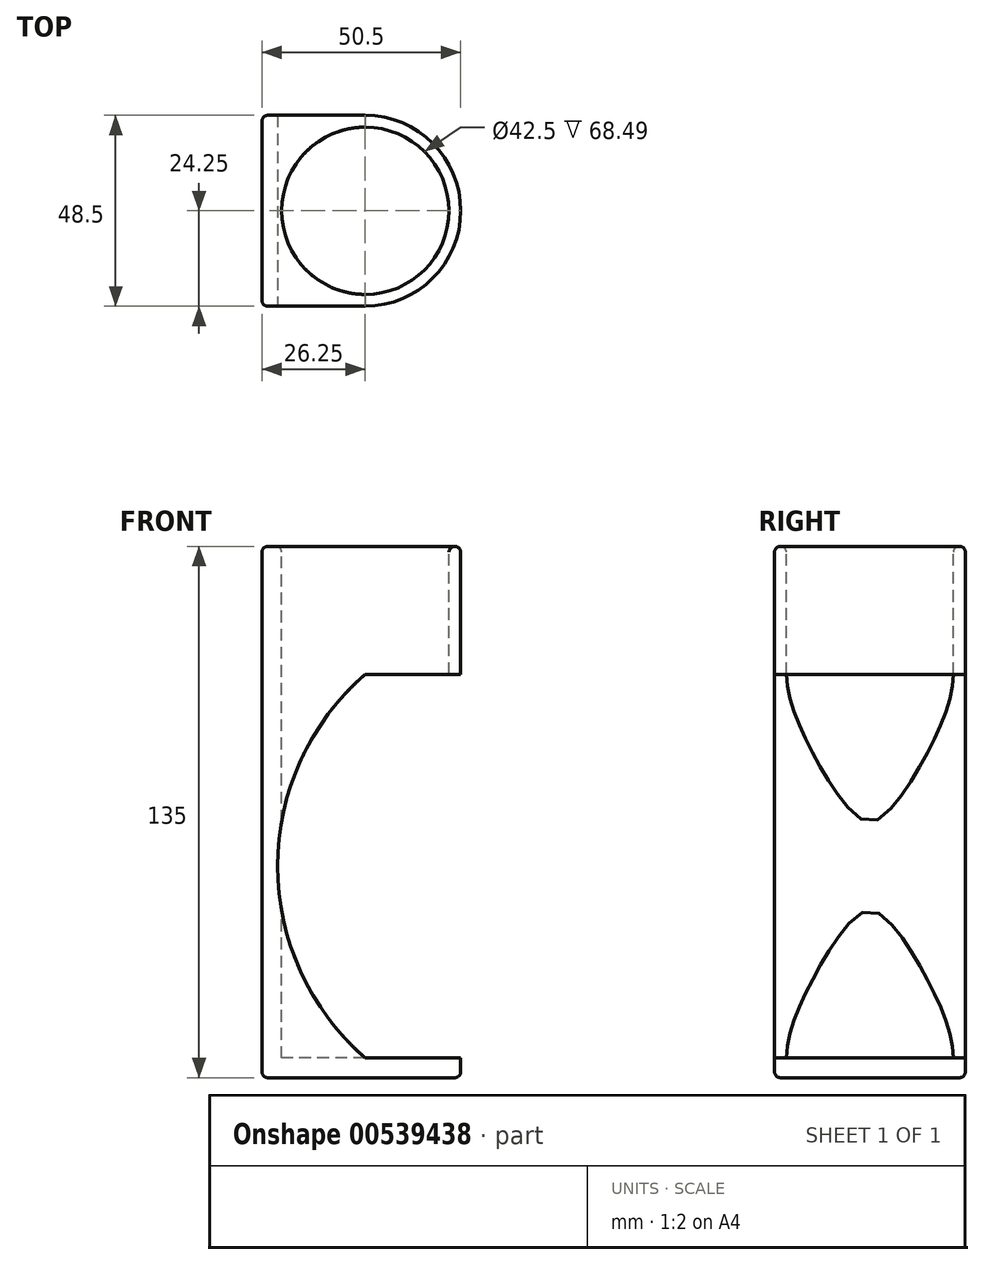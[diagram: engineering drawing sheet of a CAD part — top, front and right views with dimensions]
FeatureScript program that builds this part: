
annotation { "Feature Type Name" : "Feature", "Feature Type Description" : "" }
export const myFeature = defineFeature(function(context is Context, id is Id, definition is map)
    precondition{}
    {
        {
            var Q0;
            Q0=qCreatedBy(makeId("Top.planeOp"),FACE);
            var sketch = newSketch(context, id + "F0", { "sketchPlane" : qUnion([Q0])});
            skCircle(sketch, "E0.0", {"center": v(0, 0) * mm, "radius": 24.25 * mm});
            skLineSegment(sketch, "E1", {"start": v(-26.25, -24.25) * mm, "end": v(-26.25, 24.25) * mm});
            skLineSegment(sketch, "E2", {"start": v(-26.25, 24.25) * mm, "end": v(0, 24.25) * mm});
            skLineSegment(sketch, "E3", {"start": v(0, -24.25) * mm, "end": v(-26.25, -24.25) * mm});
            skSolve(sketch);
        }
        {
            var Q0;
            Q0 = qSketchRegion(id + "F0", true);
            extrude(context, id + "F1", {"entities" : qUnion([Q0]), "oppositeDirection" : true, "depth" : 135 * mm, "offsetDistance" : 25 * mm});
        }
        {
            var Q0;
            Q0=makeQuery(id+"F0.imprint","IMPRINT",FACE,{"disambiguationData":[TD([[makeQuery(id+"F0.imprint","IMPRINT",EDGE,{"derivedFrom":sQuery(id+"F0.wireOp",EDGE,"E1")}),-1.0]])]});
            var sketch = newSketch(context, id + "F2", { "sketchPlane" : qUnion([Q0])});
            skCircle(sketch, "E4", {"center": v(0, 0) * mm, "radius": 21.25 * mm});
            skSolve(sketch);
        }
        {
            var Q0;
            Q0 = qSketchRegion(id + "F2", true);
            extrude(context, id + "F3", {"entities" : qUnion([Q0]), "operationType" : NewBodyOperationType.REMOVE, "oppositeDirection" : true, "depth" : 130 * mm, "offsetDistance" : 25 * mm});
        }
        {
            var Q0;
            Q0=makeQuery(id+"F1.opExtrude","SWEPT_FACE",FACE,{"disambiguationData":[OSD([sQuery(id+"F0.wireOp",EDGE,"E3")])]});
            var sketch = newSketch(context, id + "F4", { "sketchPlane" : qUnion([Q0])});
            skLineSegment(sketch, "E5", {"start": v(24.25, 0) * mm, "end": v(24.25, -135) * mm});
            skLineSegment(sketch, "E6.0", {"start": v(0, -135) * mm, "end": v(0, 0) * mm});
            skLineSegment(sketch, "E7.bottom", {"start": v(0, -32.5) * mm, "end": v(24.25, -32.5) * mm});
            skLineSegment(sketch, "E7.top", {"start": v(0, -130) * mm, "end": v(24.25, -130) * mm});
            skLineSegment(sketch, "E7.left", {"start": v(0, -32.5) * mm, "end": v(0, -130) * mm});
            skLineSegment(sketch, "E7.right", {"start": v(24.25, -32.5) * mm, "end": v(24.25, -130) * mm});
            skArc(sketch, "E8", {"start": v(0, -32.5) * mm, "mid": v(-22.25, -81.25) * mm, "end": v(0, -130) * mm});
            skSolve(sketch);
        }
        {
            var Q0;
            Q0 = qSketchRegion(id + "F4", true);
            extrude(context, id + "F5", {"entities" : qUnion([Q0]), "operationType" : NewBodyOperationType.REMOVE, "oppositeDirection" : true, "depth" : 50.1 * mm, "offsetDistance" : 25 * mm, "hasSecondDirection" : true, "secondDirectionOppositeDirection" : false, "secondDirectionDepth" : 25 * mm});
        }
        {
            var Q0;
            Q0=makeQuery(id+"F1.opExtrude","CAP_FACE",FACE,{"disambiguationData":[OSD([sQuery(id+"F0.wireOp",EDGE,"E0.0"),sQuery(id+"F0.wireOp",EDGE,"E1"),sQuery(id+"F0.wireOp",EDGE,"E2"),sQuery(id+"F0.wireOp",EDGE,"E3")])],"isStart":true});
            fillet(context, id + "F6", {"entities" : qUnion([Q0]), "radius" : 1.5 * mm, "tangentPropagation" : true, "allowEdgeOverflow" : false});
        }
        {
            var Q0;
            Q0=makeQuery(id+"F1.opExtrude","SWEPT_FACE",FACE,{"disambiguationData":[OSD([sQuery(id+"F0.wireOp",EDGE,"E1")])]});
            fillet(context, id + "F7", {"entities" : qUnion([Q0]), "radius" : 1.5 * mm, "tangentPropagation" : true, "allowEdgeOverflow" : false});
        }
        {
            var Q0;
            Q0=makeQuery(id+"F1.opExtrude","CAP_FACE",FACE,{"disambiguationData":[OSD([sQuery(id+"F0.wireOp",EDGE,"E0.0"),sQuery(id+"F0.wireOp",EDGE,"E1"),sQuery(id+"F0.wireOp",EDGE,"E2"),sQuery(id+"F0.wireOp",EDGE,"E3")])],"isStart":false});
            fillet(context, id + "F8", {"entities" : qUnion([Q0]), "radius" : 1.5 * mm, "tangentPropagation" : true, "allowEdgeOverflow" : false});
        }
    });
